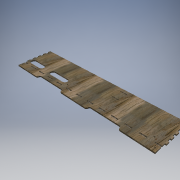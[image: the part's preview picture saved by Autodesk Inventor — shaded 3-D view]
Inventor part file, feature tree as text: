
AUTODESK INVENTOR PART (.ipt)
format: ipt  version: 2018.3 (Build 223284000, 284)  size: 393,728 bytes
history: native  units: mm
features: reference x20, other x6, extrude x4, sketch x4
ambient origin geometry x8: Origin, YZ Plane, XZ Plane, XY Plane, X Axis, Y Axis, Z Axis, Center Point
bodies: Solido1 (feature_tree)
feature tree (34):
  extrude  "Estrusione1"  Depth=95.0mm
  extrude  "Estrusione2"  TaperAngle=90.0deg  [1 undecoded]
  extrude  "Estrusione3"  Depth=95.0mm
  extrude  "Estrusione4"  Depth=5.0mm
  sketch  "Schizzo1"
  reference  "Riferimento1"
  reference  "Riferimento2"
  reference  "Riferimento3"
  reference  "Riferimento4"
  reference  "Riferimento5"
  reference  "Riferimento6"
  reference  "Riferimento7"
  reference  "Riferimento8"
  reference  "Riferimento9"
  reference  "Riferimento10"
  reference  "Riferimento11"
  reference  "Riferimento12"
  reference  "Riferimento13"
  sketch  "Schizzo2"
  reference  "Riferimento14"
  reference  "Riferimento15"
  reference  "Riferimento16"
  reference  "Riferimento17"
  sketch  "Schizzo3"
  reference  "Riferimento18"
  reference  "Riferimento19"
  reference  "Riferimento20"
  sketch  "Schizzo5"
  other  "Linea chiusa proiettata1"
  other  "<userpath>\Desktop\Scorbot Hardware\Case Board\caseHw.iam"
  other  "caseHw.iam"
  other  "tavolaBase:1"
  other  "LatoAlimentatore:1"
  other  "LatoPy:1"
note: 1 required parameter value undecoded (feature->parameter linkage not recoverable at this tier; creation-order binding heuristic only, values carry confidence <= 0.55)
